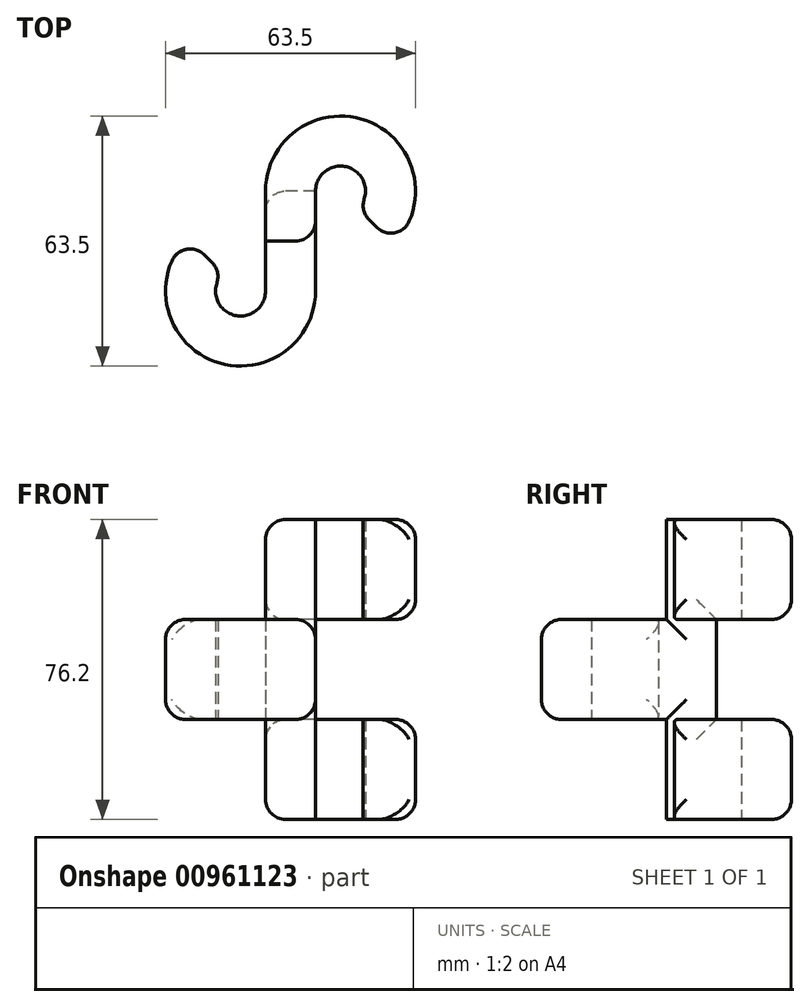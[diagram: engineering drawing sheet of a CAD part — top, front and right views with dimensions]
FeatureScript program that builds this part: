
annotation { "Feature Type Name" : "Feature", "Feature Type Description" : "" }
export const myFeature = defineFeature(function(context is Context, id is Id, definition is map)
    precondition{}
    {
        {
            var Q0;
            Q0=qCreatedBy(makeId("Top.planeOp"),FACE);
            var sketch = newSketch(context, id + "F0", { "sketchPlane" : qUnion([Q0])});
            skLineSegment(sketch, "E0", {"start": v(0, 38.1) * mm, "end": v(0, 12.7) * mm});
            skArc(sketch, "E1", {"start": v(10.84, 33.6) * mm, "mid": v(8.78, 43.97) * mm, "end": v(0, 38.1) * mm});
            skArc(sketch, "E2.0", {"start": v(19.82, 24.63) * mm, "mid": v(13.64, 55.7) * mm, "end": v(-12.7, 38.1) * mm});
            skLineSegment(sketch, "E3", {"start": v(10.84, 33.6) * mm, "end": v(19.82, 24.63) * mm});
            skArc(sketch, "E4", {"start": v(-23.54, 17.2) * mm, "mid": v(-21.48, 6.83) * mm, "end": v(-12.7, 12.7) * mm});
            skArc(sketch, "E5.0", {"start": v(-32.52, 26.17) * mm, "mid": v(-26.34, -4.9) * mm, "end": v(0, 12.7) * mm});
            skPoint(sketch, "E6.end.orphan", {"position": v(-19.05, 0) * mm});
            skPoint(sketch, "E7.orphan", {"position": v(-12.7, 12.7) * mm});
            skLineSegment(sketch, "E8", {"start": v(-23.54, 17.2) * mm, "end": v(-32.52, 26.17) * mm});
            skLineSegment(sketch, "E9", {"start": v(-12.7, 38.1) * mm, "end": v(-12.7, 12.7) * mm});
            skSolve(sketch);
        }
        {
            var Q0;
            Q0 = qSketchRegion(id + "F0", true);
            extrude(context, id + "F1", {"entities" : qUnion([Q0]), "depth" : 76.2 * mm, "offsetDistance" : 25.4 * mm});
        }
        {
            var Q0;
            Q0=makeQuery(id+"F1.opExtrude","SWEPT_FACE",FACE,{"disambiguationData":[OSD([sQuery(id+"F0.wireOp",EDGE,"E9")])]});
            var sketch = newSketch(context, id + "F2", { "sketchPlane" : qUnion([Q0])});
            skLineSegment(sketch, "E10", {"start": v(0, 0) * mm, "end": v(-38.1, 0) * mm});
            skLineSegment(sketch, "E11", {"start": v(0, 76.2) * mm, "end": v(-38.1, 76.2) * mm});
            skLineSegment(sketch, "E12.bottom", {"start": v(-38.1, 0) * mm, "end": v(-25.4, 0) * mm});
            skLineSegment(sketch, "E12.top", {"start": v(-38.1, 76.2) * mm, "end": v(-25.4, 76.2) * mm});
            skLineSegment(sketch, "E12.right", {"start": v(-25.4, 0) * mm, "end": v(-25.4, 25.4) * mm});
            skLineSegment(sketch, "E13", {"start": v(-38.1, 50.8) * mm, "end": v(-57.15, 50.8) * mm});
            skLineSegment(sketch, "E14.MirrorCS", {"start": v(-38.1, 25.4) * mm, "end": v(-57.15, 25.4) * mm});
            skLineSegment(sketch, "E15", {"start": v(-57.15, 25.4) * mm, "end": v(-57.15, 50.8) * mm});
            skLineSegment(sketch, "E16.bottom", {"start": v(-25.4, 0) * mm, "end": v(6.35, 0) * mm});
            skLineSegment(sketch, "E16.top", {"start": v(-25.4, 25.4) * mm, "end": v(6.35, 25.4) * mm});
            skLineSegment(sketch, "E16.right", {"start": v(6.35, 0) * mm, "end": v(6.35, 25.4) * mm});
            skLineSegment(sketch, "E17", {"start": v(-25.4, 50.8) * mm, "end": v(6.35, 50.8) * mm});
            skLineSegment(sketch, "E18", {"start": v(6.35, 50.8) * mm, "end": v(6.35, 76.2) * mm});
            skLineSegment(sketch, "E19", {"start": v(6.35, 76.2) * mm, "end": v(-25.4, 76.2) * mm});
            skPoint(sketch, "E20.end.orphan", {"position": v(-25.4, 38.1) * mm});
            skPoint(sketch, "E20.start.orphan", {"position": v(-38.1, 38.1) * mm});
            skLineSegment(sketch, "E21", {"start": v(-38.1, 0) * mm, "end": v(-38.1, 76.2) * mm});
            skPoint(sketch, "E22.orphan", {"position": v(-25.4, 25.4) * mm});
            skLineSegment(sketch, "E23.trimOffspring", {"start": v(-25.4, 50.8) * mm, "end": v(-25.4, 76.2) * mm});
            skSolve(sketch);
        }
        {
            var Q0;
            {var subQ0=sQuery(id+"F2.wireOp",EDGE,"E13");Q0=makeQuery(id+"F2.imprint","IMPRINT",FACE,{"disambiguationData":[TD([[makeQuery(id+"F2.imprint","IMPRINT",EDGE,{"derivedFrom":subQ0}),1.0]])]});}
            extrude(context, id + "F3", {"entities" : qUnion([Q0]), "operationType" : NewBodyOperationType.REMOVE, "endBound" : BoundingType.THROUGH_ALL, "oppositeDirection" : true, "depth" : 25.4 * mm, "offsetDistance" : 25.4 * mm});
        }
        {
            var Q0;
            Q0 = qSketchRegion(id + "F2", true);
            extrude(context, id + "F4", {"entities" : qUnion([Q0]), "operationType" : NewBodyOperationType.REMOVE, "oppositeDirection" : true, "depth" : 25.4 * mm, "offsetDistance" : 25.4 * mm});
        }
        {
            var Q0;
            Q0=makeQuery(id+"F3.boolean.opBoolean","COPY",FACE,{"disambiguationData":[TD([makeQuery(id+"F1.opExtrude","SWEPT_FACE",FACE,{"disambiguationData":[OSD([sQuery(id+"F0.wireOp",EDGE,"E1")])]}),makeQuery(id+"F1.opExtrude","SWEPT_FACE",FACE,{"disambiguationData":[OSD([sQuery(id+"F0.wireOp",EDGE,"E2.0")])]}),makeQuery(id+"F3.opExtrude","SWEPT_FACE",FACE,{"disambiguationData":[OSD([sQuery(id+"F2.wireOp",EDGE,"E13")])]}),makeQuery(id+"F3.opExtrude","SWEPT_FACE",FACE,{"disambiguationData":[OSD([sQuery(id+"F2.wireOp",EDGE,"E14.MirrorCS")])]})])],"derivedFrom":makeQuery(id+"F3.opExtrude","SWEPT_FACE",FACE,{"disambiguationData":[OSD([sQuery(id+"F2.wireOp",EDGE,"E21")])]})});
            var sketch = newSketch(context, id + "F5", { "sketchPlane" : qUnion([Q0])});
            skLineSegment(sketch, "E24.bottom", {"start": v(-25.4, 50.8) * mm, "end": v(-9.42, 50.8) * mm});
            skLineSegment(sketch, "E24.top", {"start": v(-25.4, 25.4) * mm, "end": v(-9.42, 25.4) * mm});
            skLineSegment(sketch, "E24.left", {"start": v(-25.4, 50.8) * mm, "end": v(-25.4, 25.4) * mm});
            skLineSegment(sketch, "E24.right", {"start": v(-9.42, 50.8) * mm, "end": v(-9.42, 25.4) * mm});
            skSolve(sketch);
        }
        {
            var Q0;
            Q0 = qSketchRegion(id + "F5", true);
            extrude(context, id + "F6", {"entities" : qUnion([Q0]), "operationType" : NewBodyOperationType.REMOVE, "endBound" : BoundingType.THROUGH_ALL, "oppositeDirection" : true, "depth" : 25.4 * mm, "offsetDistance" : 25.4 * mm});
        }
        {
            var Q0;
            Q0=makeQuery(id+"F4.boolean.opBoolean","COPY",FACE,{"derivedFrom":makeQuery(id+"F4.opExtrude","CAP_FACE",FACE,{"disambiguationData":[OSD([sQuery(id+"F2.wireOp",EDGE,"E17"),sQuery(id+"F2.wireOp",EDGE,"E18"),sQuery(id+"F2.wireOp",EDGE,"E19"),sQuery(id+"F2.wireOp",EDGE,"E23.trimOffspring")])],"isStart":true})});
            var sketch = newSketch(context, id + "F7", { "sketchPlane" : qUnion([Q0])});
            skLineSegment(sketch, "E25.bottom", {"start": v(17.29, 76.2) * mm, "end": v(-6.4, 76.2) * mm});
            skLineSegment(sketch, "E25.top", {"start": v(17.29, 50.8) * mm, "end": v(-6.4, 50.8) * mm});
            skLineSegment(sketch, "E25.left", {"start": v(17.29, 76.2) * mm, "end": v(17.29, 50.8) * mm});
            skLineSegment(sketch, "E25.right", {"start": v(-6.4, 76.2) * mm, "end": v(-6.4, 50.8) * mm});
            skLineSegment(sketch, "E26.MirrorCS", {"start": v(17.29, 0) * mm, "end": v(17.29, 25.4) * mm});
            skLineSegment(sketch, "E27.MirrorCS", {"start": v(17.29, 25.4) * mm, "end": v(-6.4, 25.4) * mm});
            skLineSegment(sketch, "E28.MirrorCS", {"start": v(-6.4, 0) * mm, "end": v(-6.4, 25.4) * mm});
            skLineSegment(sketch, "E29.MirrorCS", {"start": v(17.29, 0) * mm, "end": v(-6.4, 0) * mm});
            skSolve(sketch);
        }
        {
            var Q0;
            Q0 = qSketchRegion(id + "F7", true);
            extrude(context, id + "F8", {"entities" : qUnion([Q0]), "operationType" : NewBodyOperationType.REMOVE, "endBound" : BoundingType.THROUGH_ALL, "oppositeDirection" : true, "depth" : 25.4 * mm, "offsetDistance" : 25.4 * mm});
        }
        {
            var Q0;
            Q0=makeQuery(id+"F8.boolean.opBoolean","COPY",FACE,{"derivedFrom":makeQuery(id+"F8.opExtrude","SWEPT_FACE",FACE,{"disambiguationData":[OSD([sQuery(id+"F7.wireOp",EDGE,"E25.left")])]})});
            var sketch = newSketch(context, id + "F9", { "sketchPlane" : qUnion([Q0])});
            skLineSegment(sketch, "E30", {"start": v(-37.54, 76.2) * mm, "end": v(-37.54, 50.8) * mm});
            skLineSegment(sketch, "E31", {"start": v(-37.54, 50.8) * mm, "end": v(-23.64, 50.8) * mm});
            skLineSegment(sketch, "E32", {"start": v(-23.64, 50.8) * mm, "end": v(-23.64, 76.2) * mm});
            skLineSegment(sketch, "E33", {"start": v(-23.64, 76.2) * mm, "end": v(-37.54, 76.2) * mm});
            skLineSegment(sketch, "E34.MirrorCS", {"start": v(-37.54, 25.4) * mm, "end": v(-23.64, 25.4) * mm});
            skLineSegment(sketch, "E35.MirrorCS", {"start": v(-37.54, 0) * mm, "end": v(-37.54, 25.4) * mm});
            skLineSegment(sketch, "E36.MirrorCS", {"start": v(-23.64, 25.4) * mm, "end": v(-23.64, 0) * mm});
            skLineSegment(sketch, "E37.MirrorCS", {"start": v(-23.64, 0) * mm, "end": v(-37.54, 0) * mm});
            skSolve(sketch);
        }
        {
            var Q0;
            Q0 = qSketchRegion(id + "F9", true);
            extrude(context, id + "F10", {"entities" : qUnion([Q0]), "operationType" : NewBodyOperationType.REMOVE, "endBound" : BoundingType.THROUGH_ALL, "oppositeDirection" : true, "depth" : 25.4 * mm, "offsetDistance" : 25.4 * mm});
        }
        {
            var Q0;
            Q0=makeQuery(id+"F4.boolean.opBoolean","INTERSECT",EDGE,{"derivedFrom":[makeQuery(id+"F1.opExtrude","SWEPT_FACE",FACE,{"disambiguationData":[OSD([sQuery(id+"F0.wireOp",EDGE,"E0")])]}),makeQuery(id+"F4.opExtrude","SWEPT_FACE",FACE,{"disambiguationData":[OSD([sQuery(id+"F2.wireOp",EDGE,"E12.right")])]})]});
            var Q1;
            Q1=makeQuery(id+"F4.boolean.opBoolean","COPY",EDGE,{"derivedFrom":makeQuery(id+"F4.opExtrude","CAP_EDGE",EDGE,{"disambiguationData":[OSD([sQuery(id+"F2.wireOp",EDGE,"E12.right")])],"isStart":true})});
            var Q2;
            Q2=makeQuery(id+"F4.boolean.opBoolean","INTERSECT",EDGE,{"derivedFrom":[makeQuery(id+"F1.opExtrude","SWEPT_FACE",FACE,{"disambiguationData":[OSD([sQuery(id+"F0.wireOp",EDGE,"E0")])]}),makeQuery(id+"F4.opExtrude","SWEPT_FACE",FACE,{"disambiguationData":[OSD([sQuery(id+"F2.wireOp",EDGE,"E23.trimOffspring")])]})]});
            var Q3;
            Q3=makeQuery(id+"F4.boolean.opBoolean","COPY",EDGE,{"derivedFrom":makeQuery(id+"F4.opExtrude","CAP_EDGE",EDGE,{"disambiguationData":[OSD([sQuery(id+"F2.wireOp",EDGE,"E23.trimOffspring")])],"isStart":true})});
            var Q4;
            {var subQ0=sQuery(id+"F0.wireOp",EDGE,"E0");Q4=makeQuery(id+"F3.boolean.opBoolean","SPLIT",EDGE,{"disambiguationData":[topologyDisambiguationEdgeConnected([makeQuery(id+"F1.opExtrude","SWEPT_FACE",FACE,{"disambiguationData":[OSD([subQ0])]}),makeQuery(id+"F3.opExtrude","SWEPT_FACE",FACE,{"disambiguationData":[OSD([sQuery(id+"F2.wireOp",EDGE,"E21")])]})])],"derivedFrom":makeQuery(id+"F1.opExtrude","SWEPT_EDGE",EDGE,{"disambiguationData":[OSD([subQ0,sQuery(id+"F0.wireOp",EDGE,"E1")])]})});}
            var Q5;
            Q5=makeQuery(id+"F3.boolean.opBoolean","MERGE",EDGE,{"derivedFrom":[makeQuery(id+"F1.opExtrude","SWEPT_EDGE",EDGE,{"disambiguationData":[OSD([sQuery(id+"F0.wireOp",EDGE,"E2.0"),sQuery(id+"F0.wireOp",EDGE,"E9")])]})],"fromTools":[makeQuery(id+"F3.opExtrude","CAP_EDGE",EDGE,{"disambiguationData":[OSD([sQuery(id+"F2.wireOp",EDGE,"E21")])],"isStart":true})]});
            var Q6;
            {var subQ0=sQuery(id+"F0.wireOp",EDGE,"E3");var subQ1=sQuery(id+"F0.wireOp",EDGE,"E2.0");Q6=makeQuery(id+"F6.boolean.opBoolean","SPLIT",EDGE,{"disambiguationData":[TD([makeQuery(id+"F3.boolean.opBoolean","COPY",FACE,{"derivedFrom":makeQuery(id+"F3.opExtrude","SWEPT_FACE",FACE,{"disambiguationData":[OSD([sQuery(id+"F2.wireOp",EDGE,"E14.MirrorCS")])]})})])],"derivedFrom":makeQuery(id+"F1.opExtrude","SWEPT_EDGE",EDGE,{"disambiguationData":[OSD([subQ1,subQ0])]})});}
            var Q7;
            {var subQ0=sQuery(id+"F0.wireOp",EDGE,"E3");var subQ1=sQuery(id+"F0.wireOp",EDGE,"E1");Q7=makeQuery(id+"F6.boolean.opBoolean","SPLIT",EDGE,{"disambiguationData":[TD([makeQuery(id+"F3.boolean.opBoolean","COPY",FACE,{"derivedFrom":makeQuery(id+"F3.opExtrude","SWEPT_FACE",FACE,{"disambiguationData":[OSD([sQuery(id+"F2.wireOp",EDGE,"E14.MirrorCS")])]})})])],"derivedFrom":makeQuery(id+"F1.opExtrude","SWEPT_EDGE",EDGE,{"disambiguationData":[OSD([subQ1,subQ0])]})});}
            var Q8;
            {var subQ0=sQuery(id+"F0.wireOp",EDGE,"E3");var subQ1=sQuery(id+"F0.wireOp",EDGE,"E2.0");Q8=makeQuery(id+"F6.boolean.opBoolean","SPLIT",EDGE,{"disambiguationData":[TD([makeQuery(id+"F3.boolean.opBoolean","COPY",FACE,{"derivedFrom":makeQuery(id+"F3.opExtrude","SWEPT_FACE",FACE,{"disambiguationData":[OSD([sQuery(id+"F2.wireOp",EDGE,"E13")])]})})])],"derivedFrom":makeQuery(id+"F1.opExtrude","SWEPT_EDGE",EDGE,{"disambiguationData":[OSD([subQ1,subQ0])]})});}
            var Q9;
            {var subQ0=sQuery(id+"F0.wireOp",EDGE,"E3");var subQ1=sQuery(id+"F0.wireOp",EDGE,"E1");Q9=makeQuery(id+"F6.boolean.opBoolean","SPLIT",EDGE,{"disambiguationData":[TD([makeQuery(id+"F3.boolean.opBoolean","COPY",FACE,{"derivedFrom":makeQuery(id+"F3.opExtrude","SWEPT_FACE",FACE,{"disambiguationData":[OSD([sQuery(id+"F2.wireOp",EDGE,"E13")])]})})])],"derivedFrom":makeQuery(id+"F1.opExtrude","SWEPT_EDGE",EDGE,{"disambiguationData":[OSD([subQ1,subQ0])]})});}
            var Q10;
            Q10=makeQuery(id+"F1.opExtrude","SWEPT_EDGE",EDGE,{"disambiguationData":[OSD([sQuery(id+"F0.wireOp",EDGE,"E5.0"),sQuery(id+"F0.wireOp",EDGE,"E8")])]});
            var Q11;
            Q11=makeQuery(id+"F1.opExtrude","SWEPT_EDGE",EDGE,{"disambiguationData":[OSD([sQuery(id+"F0.wireOp",EDGE,"E4"),sQuery(id+"F0.wireOp",EDGE,"E8")])]});
            var Q12;
            Q12=makeQuery(id+"F10.boolean.opBoolean","INTERSECT",EDGE,{"derivedFrom":[makeQuery(id+"F1.opExtrude","SWEPT_FACE",FACE,{"disambiguationData":[OSD([sQuery(id+"F0.wireOp",EDGE,"E5.0")])]}),makeQuery(id+"F10.opExtrude","SWEPT_FACE",FACE,{"disambiguationData":[OSD([sQuery(id+"F9.wireOp",EDGE,"E31")])]})]});
            var Q13;
            Q13=makeQuery(id+"F10.boolean.opBoolean","INTERSECT",EDGE,{"derivedFrom":[makeQuery(id+"F1.opExtrude","SWEPT_FACE",FACE,{"disambiguationData":[OSD([sQuery(id+"F0.wireOp",EDGE,"E5.0")])]}),makeQuery(id+"F10.opExtrude","SWEPT_FACE",FACE,{"disambiguationData":[OSD([sQuery(id+"F9.wireOp",EDGE,"E34.MirrorCS")])]})]});
            var Q14;
            Q14=makeQuery(id+"F1.opExtrude","CAP_EDGE",EDGE,{"disambiguationData":[OSD([sQuery(id+"F0.wireOp",EDGE,"E2.0")])],"isStart":true});
            var Q15;
            Q15=makeQuery(id+"F6.boolean.opBoolean","INTERSECT",EDGE,{"derivedFrom":[makeQuery(id+"F1.opExtrude","SWEPT_FACE",FACE,{"disambiguationData":[OSD([sQuery(id+"F0.wireOp",EDGE,"E2.0")])]}),makeQuery(id+"F6.opExtrude","SWEPT_FACE",FACE,{"disambiguationData":[OSD([sQuery(id+"F5.wireOp",EDGE,"E24.top")])]})]});
            var Q16;
            Q16=makeQuery(id+"F1.opExtrude","CAP_EDGE",EDGE,{"disambiguationData":[OSD([sQuery(id+"F0.wireOp",EDGE,"E2.0")])],"isStart":false});
            var Q17;
            Q17=makeQuery(id+"F6.boolean.opBoolean","INTERSECT",EDGE,{"derivedFrom":[makeQuery(id+"F1.opExtrude","SWEPT_FACE",FACE,{"disambiguationData":[OSD([sQuery(id+"F0.wireOp",EDGE,"E2.0")])]}),makeQuery(id+"F6.opExtrude","SWEPT_FACE",FACE,{"disambiguationData":[OSD([sQuery(id+"F5.wireOp",EDGE,"E24.bottom")])]})]});
            fillet(context, id + "F11", {"entities" : qUnion([Q0, Q1, Q2, Q3, Q4, Q5, Q6, Q7, Q8, Q9, Q10, Q11, Q12, Q13, Q14, Q15, Q16, Q17]), "radius" : 5.08 * mm, "tangentPropagation" : true, "allowEdgeOverflow" : false});
        }
    });
